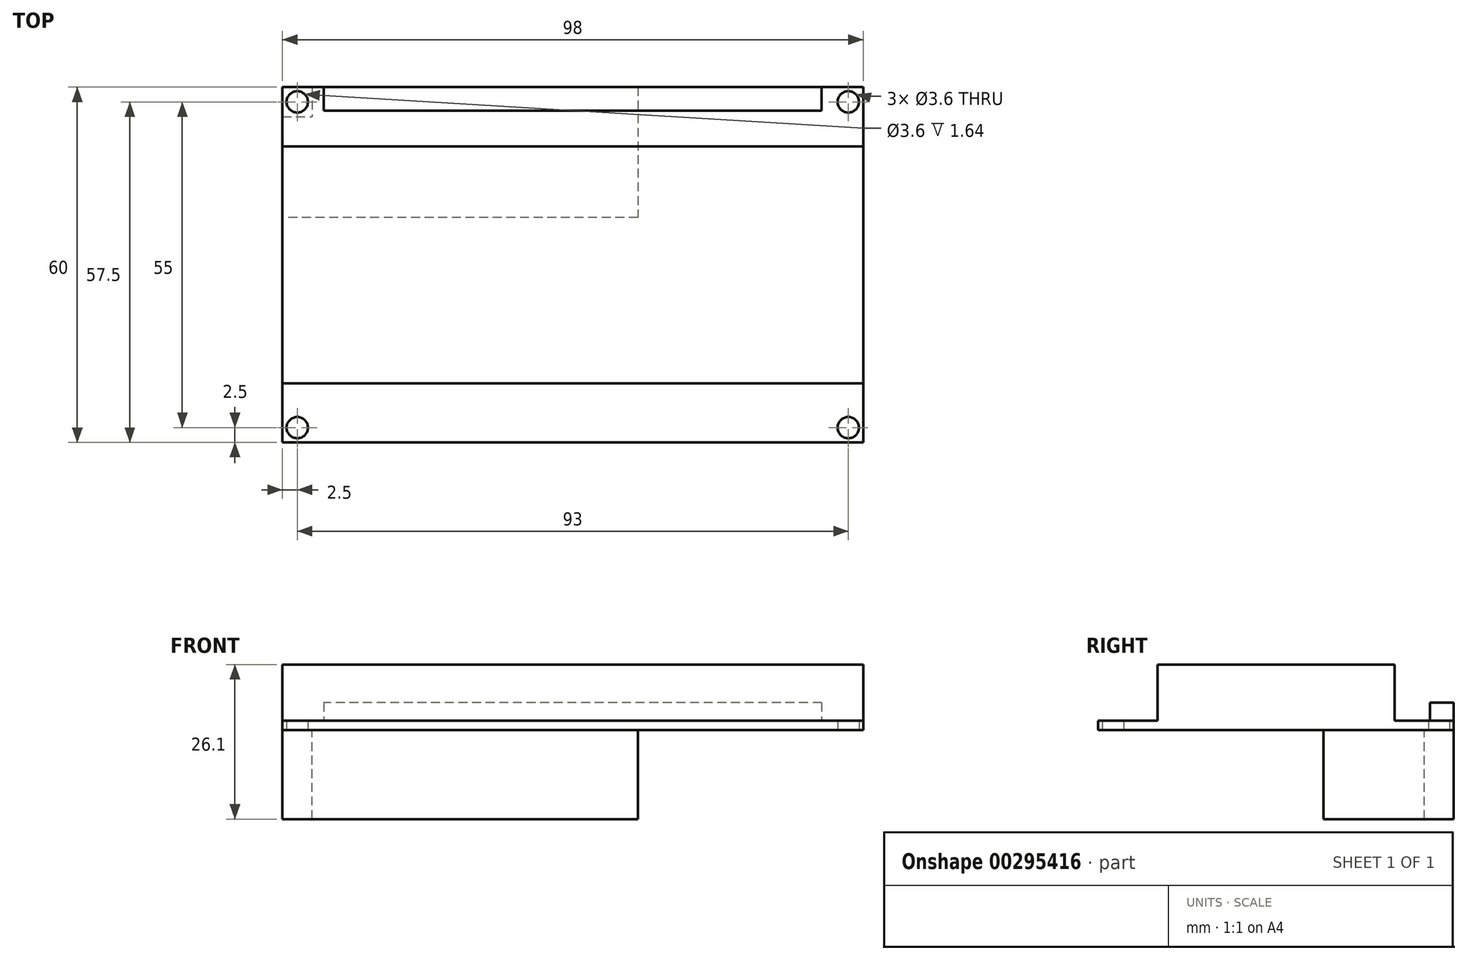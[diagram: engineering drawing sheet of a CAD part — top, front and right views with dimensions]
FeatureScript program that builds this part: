
annotation { "Feature Type Name" : "Feature", "Feature Type Description" : "" }
export const myFeature = defineFeature(function(context is Context, id is Id, definition is map)
    precondition{}
    {
        {
            var Q0;
            Q0=qCreatedBy(makeId("Top.planeOp"),FACE);
            var sketch = newSketch(context, id + "F0", { "sketchPlane" : qUnion([Q0])});
            skLineSegment(sketch, "E0.bottom", {"start": v(49, -30) * mm, "end": v(-49, -30) * mm});
            skLineSegment(sketch, "E0.top", {"start": v(49, 30) * mm, "end": v(-49, 30) * mm});
            skLineSegment(sketch, "E0.left", {"start": v(49, -30) * mm, "end": v(49, 30) * mm});
            skLineSegment(sketch, "E0.right", {"start": v(-49, -30) * mm, "end": v(-49, 30) * mm});
            skPoint(sketch, "E0.middle", {"position": v(0, 0) * mm});
            skCircle(sketch, "E1", {"center": v(46.5, 27.5) * mm, "radius": 1.8 * mm});
            skCircle(sketch, "E2.MirrorC", {"center": v(46.5, -27.5) * mm, "radius": 1.8 * mm});
            skCircle(sketch, "E3.MirrorC", {"center": v(-46.5, -27.5) * mm, "radius": 1.8 * mm});
            skCircle(sketch, "E4.MirrorC", {"center": v(-46.5, 27.5) * mm, "radius": 1.8 * mm});
            skSolve(sketch);
        }
        {
            var Q0;
            Q0 = qSketchRegion(id + "F0", true);
            extrude(context, id + "F1", {"entities" : qUnion([Q0]), "depth" : 1.64 * mm});
        }
        {
            var Q0;
            Q0=makeQuery(id+"F1.opExtrude","CAP_FACE",FACE,{"disambiguationData":[OSD([sQuery(id+"F0.wireOp",EDGE,"E0.bottom"),sQuery(id+"F0.wireOp",EDGE,"E0.top"),sQuery(id+"F0.wireOp",EDGE,"E0.left"),sQuery(id+"F0.wireOp",EDGE,"E0.right"),sQuery(id+"F0.wireOp",EDGE,"E1"),sQuery(id+"F0.wireOp",EDGE,"E2.MirrorC"),sQuery(id+"F0.wireOp",EDGE,"E3.MirrorC"),sQuery(id+"F0.wireOp",EDGE,"E4.MirrorC")])],"isStart":false});
            var sketch = newSketch(context, id + "F2", { "sketchPlane" : qUnion([Q0])});
            skLineSegment(sketch, "E5.0", {"start": v(49, -30) * mm, "end": v(49, 30) * mm});
            skLineSegment(sketch, "E6.0", {"start": v(-49, -30) * mm, "end": v(-49, 30) * mm});
            skLineSegment(sketch, "E7", {"start": v(49, 20) * mm, "end": v(-49, 20) * mm});
            skLineSegment(sketch, "E8", {"start": v(49, -20) * mm, "end": v(-49, -20) * mm});
            skSolve(sketch);
        }
        {
            var Q0;
            Q0 = qSketchRegion(id + "F2", true);
            extrude(context, id + "F3", {"entities" : qUnion([Q0]), "operationType" : NewBodyOperationType.ADD, "depth" : (11.1 - 1.64) * mm});
        }
        {
            var Q0;
            {var subQ0=sQuery(id+"F0.wireOp",EDGE,"E1");var subQ1=sQuery(id+"F0.wireOp",EDGE,"E0.right");var subQ2=sQuery(id+"F0.wireOp",EDGE,"E0.left");var subQ3=sQuery(id+"F0.wireOp",EDGE,"E0.top");var subQ4=sQuery(id+"F0.wireOp",EDGE,"E4.MirrorC");Q0=makeQuery(id+"F3.boolean.opBoolean","SPLIT",FACE,{"disambiguationData":[TD([makeQuery(id+"F1.opExtrude","SWEPT_FACE",FACE,{"disambiguationData":[OSD([subQ3])]})])],"derivedFrom":makeQuery(id+"F1.opExtrude","CAP_FACE",FACE,{"disambiguationData":[OSD([sQuery(id+"F0.wireOp",EDGE,"E0.bottom"),subQ3,subQ2,subQ1,subQ0,sQuery(id+"F0.wireOp",EDGE,"E2.MirrorC"),sQuery(id+"F0.wireOp",EDGE,"E3.MirrorC"),subQ4])],"isStart":false})});}
            var sketch = newSketch(context, id + "F4", { "sketchPlane" : qUnion([Q0])});
            skLineSegment(sketch, "E9.0", {"start": v(42, 30) * mm, "end": v(-42, 30) * mm});
            skLineSegment(sketch, "E10", {"start": v(-42, 30) * mm, "end": v(-42, 26) * mm});
            skLineSegment(sketch, "E11.MirrorCS", {"start": v(42, 30) * mm, "end": v(42, 26) * mm});
            skLineSegment(sketch, "E12", {"start": v(-42, 26) * mm, "end": v(42, 26) * mm});
            skPoint(sketch, "E13.orphan", {"position": v(-49, 30) * mm});
            skPoint(sketch, "E14.orphan", {"position": v(49, 30) * mm});
            skSolve(sketch);
        }
        {
            var Q0;
            Q0 = qSketchRegion(id + "F4", true);
            extrude(context, id + "F5", {"entities" : qUnion([Q0]), "operationType" : NewBodyOperationType.ADD, "depth" : 3 * mm});
        }
        {
            var Q0;
            Q0=makeQuery(id+"F1.opExtrude","CAP_FACE",FACE,{"disambiguationData":[OSD([sQuery(id+"F0.wireOp",EDGE,"E0.bottom"),sQuery(id+"F0.wireOp",EDGE,"E0.top"),sQuery(id+"F0.wireOp",EDGE,"E0.left"),sQuery(id+"F0.wireOp",EDGE,"E0.right"),sQuery(id+"F0.wireOp",EDGE,"E1"),sQuery(id+"F0.wireOp",EDGE,"E2.MirrorC"),sQuery(id+"F0.wireOp",EDGE,"E3.MirrorC"),sQuery(id+"F0.wireOp",EDGE,"E4.MirrorC")])],"isStart":true});
            var sketch = newSketch(context, id + "F6", { "sketchPlane" : qUnion([Q0])});
            skLineSegment(sketch, "E15.0", {"start": v(-49, -8) * mm, "end": v(-49, -25) * mm});
            skLineSegment(sketch, "E16.0", {"start": v(11, -30) * mm, "end": v(-44, -30) * mm});
            skLineSegment(sketch, "E17", {"start": v(11, -30) * mm, "end": v(11, -8) * mm});
            skLineSegment(sketch, "E18", {"start": v(11, -8) * mm, "end": v(-49, -8) * mm});
            skPoint(sketch, "E19.orphan", {"position": v(49, -30) * mm});
            skPoint(sketch, "E20.orphan", {"position": v(-49, 30) * mm});
            skLineSegment(sketch, "E21.top", {"start": v(-49, -25) * mm, "end": v(-44, -25) * mm});
            skLineSegment(sketch, "E21.right", {"start": v(-44, -30) * mm, "end": v(-44, -25) * mm});
            skCircle(sketch, "E22.0", {"center": v(-46.5, -27.5) * mm, "radius": 1.8 * mm, "construction": true});
            skCircle(sketch, "E23", {"center": v(-46.5, -27.5) * mm, "radius": 2.5 * mm, "construction": true});
            skPoint(sketch, "E24.orphan", {"position": v(-49, -30) * mm});
            skSolve(sketch);
        }
        {
            var Q0;
            Q0 = qSketchRegion(id + "F6", true);
            extrude(context, id + "F7", {"entities" : qUnion([Q0]), "operationType" : NewBodyOperationType.ADD, "depth" : 15 * mm});
        }
    });
